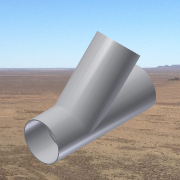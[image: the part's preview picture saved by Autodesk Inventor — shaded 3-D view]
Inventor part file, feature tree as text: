
AUTODESK INVENTOR PART (.ipt)
format: ipt  version: 2013 SP2 (Build 170200200, 200)  size: 221,696 bytes
history: native  units: in
note: dims shown in document units (in); Inventor stores cm internally (conversion verified against a paired STEP export)
features: sketch x9, extrude x7, plane x3
ambient origin geometry x8: Origin, YZ Plane, XZ Plane, XY Plane, X Axis, Y Axis, Z Axis, Center Point
bodies: Solid1 (feature_tree)
feature tree (19):
  extrude  "Extrusion1"  Depth=6.875in TaperAngle=0.0deg
  extrude  "Extrusion2"  Depth=6.875in TaperAngle=0.0deg
  extrude  "Extrusion3"  Depth=1.5in TaperAngle=0.0deg
  extrude  "Extrusion4"  Depth=1.5in TaperAngle=0.0deg
  sketch  "Sketch5"  dims[d14=-1.25in d15=2.156in]
  plane  "Work Plane2"
  sketch  "Sketch6"  dims[d16=45.0deg d18=2.5in]
  plane  "Work Plane3"
  extrude  "Extrusion5"  Depth=2.156in
  extrude  "Extrusion6"  Depth=2.5in
  extrude  "Extrusion8"  Depth=2.375in
  sketch  "Sketch1"  dims[d0=2.5in d1=6.875in d2=0.0in]
  sketch  "Sketch2"  dims[d3=2.067in d5=6.875in d6=0.0in]
  sketch  "Sketch3"  dims[d7=2.375in d9=1.5in d10=0.0in]
  sketch  "Sketch4"  dims[d11=2.375in d12=1.5in d13=0.0in]
  plane  "Work Plane1"
  sketch  "Sketch7"  dims[d19=4.7in d20=0.0in d21=2.375in]
  sketch  "Sketch8"  dims[d22=1.4in d23=0.0in]
  sketch  "Sketch9"  dims[d24=2.06in d27=1.4in d28=0.0in]
